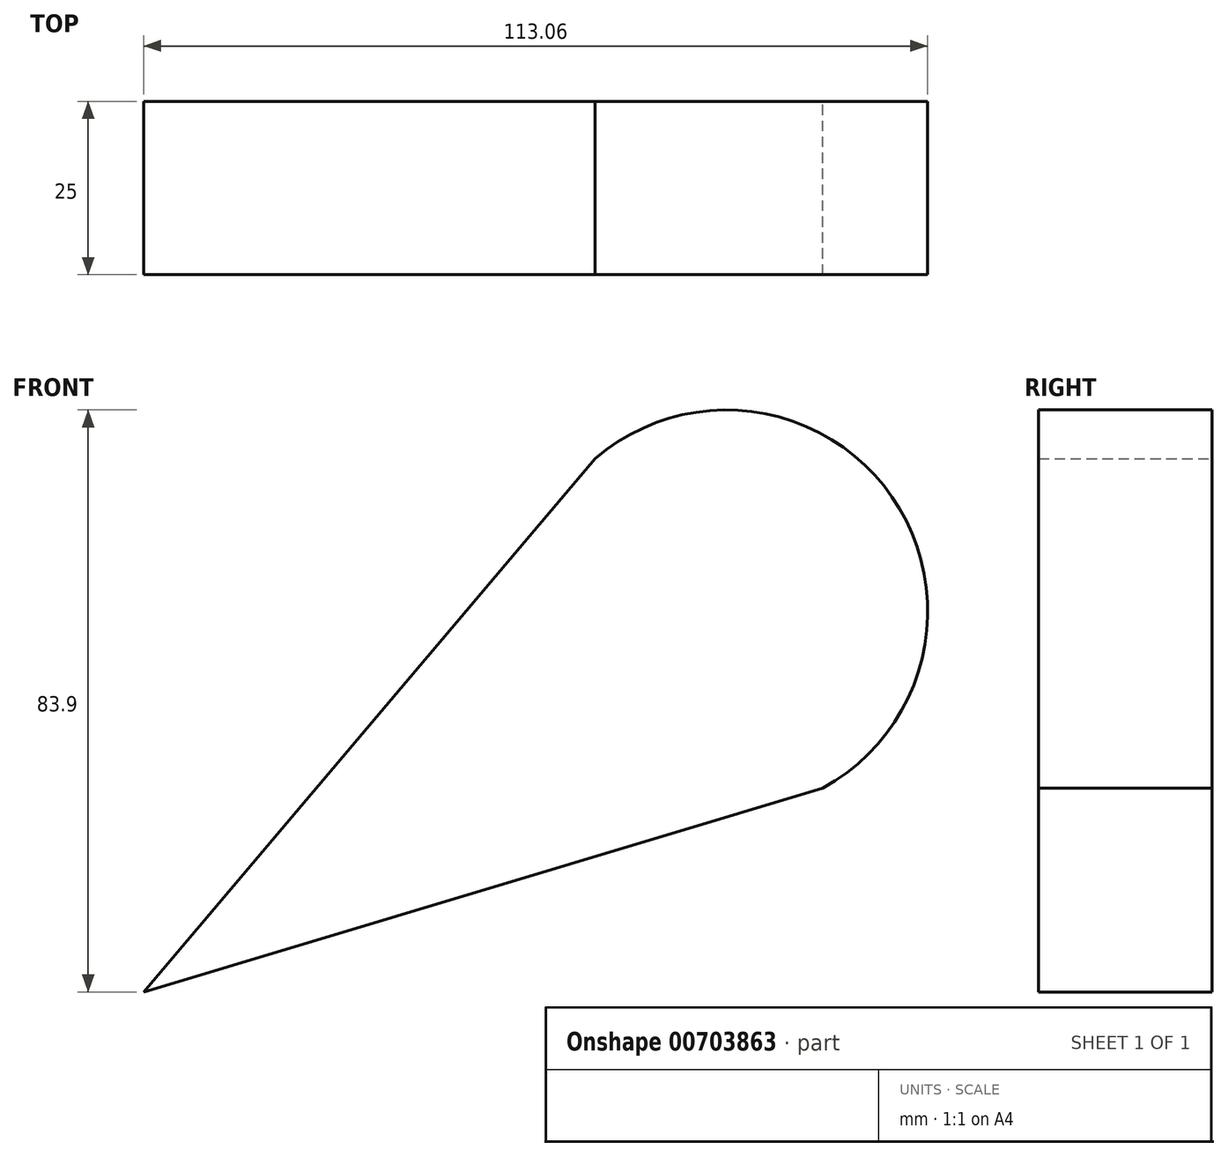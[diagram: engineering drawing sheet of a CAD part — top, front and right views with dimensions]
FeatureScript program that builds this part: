
annotation { "Feature Type Name" : "Feature", "Feature Type Description" : "" }
export const myFeature = defineFeature(function(context is Context, id is Id, definition is map)
    precondition{}
    {
        {
            var Q0;
            Q0=qCreatedBy(makeId("Front.planeOp"),FACE);
            var sketch = newSketch(context, id + "F0", { "sketchPlane" : qUnion([Q0])});
            skArc(sketch, "E0", {"start": v(0, 28.68) * mm, "mid": v(58.03, 29.6) * mm, "end": v(0, 30.54) * mm});
            skLineSegment(sketch, "E1", {"start": v(10.08, 51.61) * mm, "end": v(-55.03, -25.27) * mm});
            skLineSegment(sketch, "E2", {"start": v(-55.03, -25.27) * mm, "end": v(42.88, 4.12) * mm});
            skSolve(sketch);
        }
        {
            var Q0;
            Q0=qCreatedBy(makeId("Front.planeOp"),FACE);
            var sketch = newSketch(context, id + "F1", { "sketchPlane" : qUnion([Q0])});
            skSolve(sketch);
        }
        {
            var Q0;
            Q0 = qSketchRegion(id + "F1", true);
            var Q1;
            {var subQ1=sQuery(id+"F0.wireOp",EDGE,"E1");var subQ3=sQuery(id+"F0.wireOp",EDGE,"E0");var subQ6=makeQuery(id+"F0.imprint","INTERSECT",VERTEX,{"disambiguationData":[OD(0.0)],"derivedFrom":[subQ3,subQ1]});Q1=makeQuery(id+"F0.imprint","IMPRINT",FACE,{"disambiguationData":[TD([[makeQuery(id+"F0.imprint","IMPRINT",EDGE,{"disambiguationData":[TD([[subQ6,1.0]])],"derivedFrom":subQ3}),1.0]])]});}
            extrude(context, id + "F2", {"entities" : qUnion([Q0, Q1]), "depth" : 25 * mm, "offsetDistance" : 25 * mm});
        }
    });
